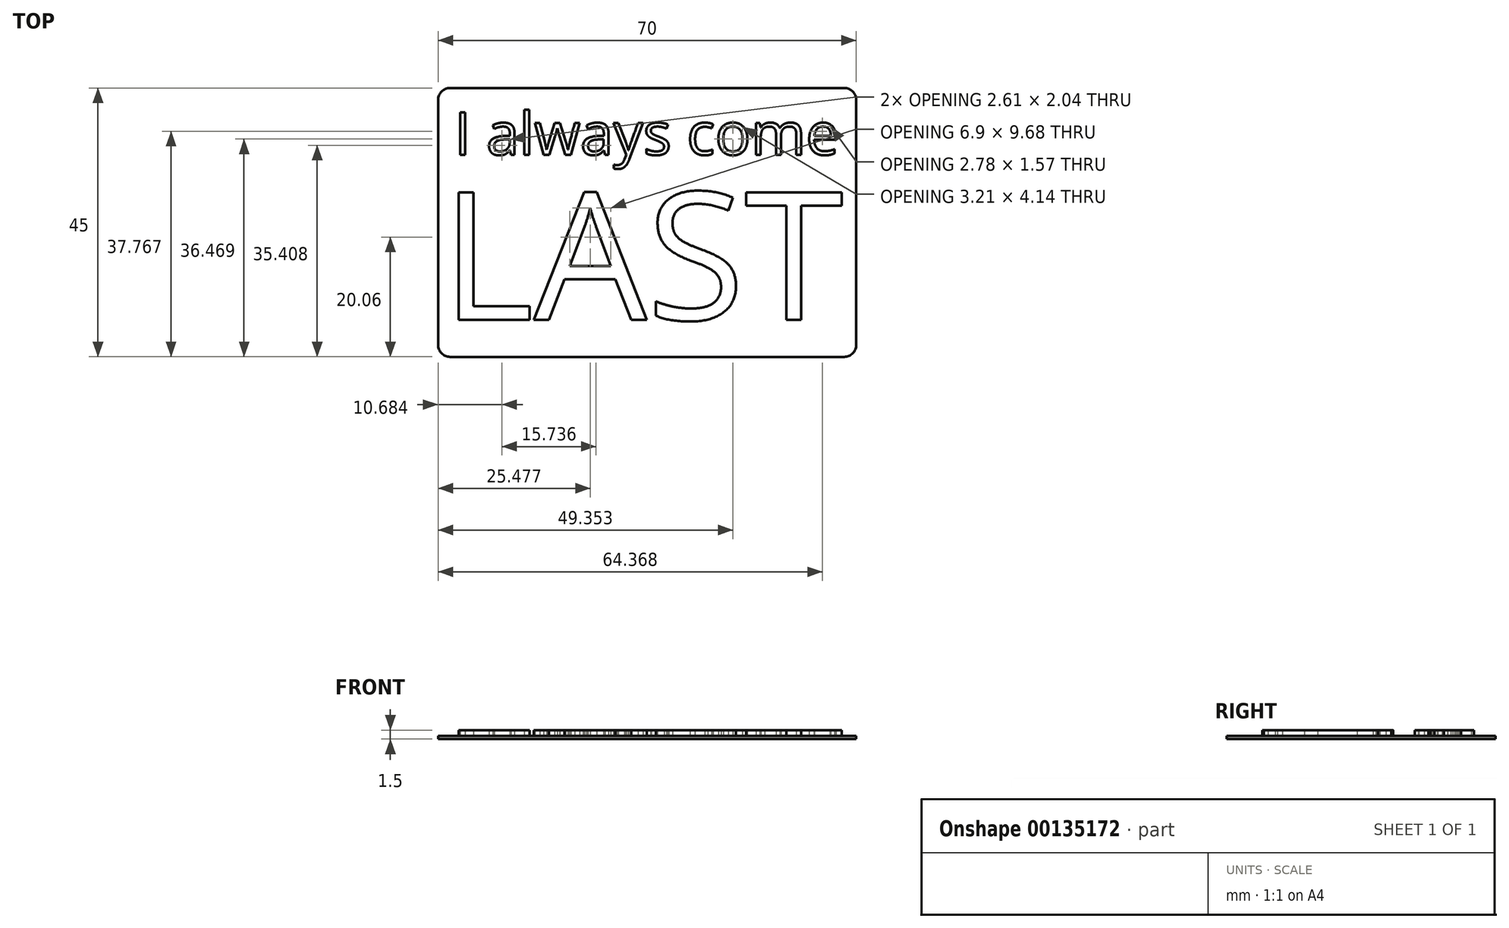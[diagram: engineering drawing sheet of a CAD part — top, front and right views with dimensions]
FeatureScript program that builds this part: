
annotation { "Feature Type Name" : "Feature", "Feature Type Description" : "" }
export const myFeature = defineFeature(function(context is Context, id is Id, definition is map)
    precondition{}
    {
        {
            var Q0;
            Q0=qCreatedBy(makeId("Top.planeOp"),FACE);
            var sketch = newSketch(context, id + "F0", { "sketchPlane" : qUnion([Q0])});
            skLineSegment(sketch, "E0.bottom", {"start": v(-20.28, 6.49) * mm, "end": v(49.72, 6.49) * mm});
            skLineSegment(sketch, "E0.top", {"start": v(-20.28, -38.51) * mm, "end": v(49.72, -38.51) * mm});
            skLineSegment(sketch, "E0.left", {"start": v(-20.28, 6.49) * mm, "end": v(-20.28, -38.51) * mm});
            skLineSegment(sketch, "E0.right", {"start": v(49.72, 6.49) * mm, "end": v(49.72, -38.51) * mm});
            skSolve(sketch);
        }
        {
            var Q0;
            Q0=makeQuery(id+"F0.imprint","IMPRINT",FACE,{"disambiguationData":[TD([[makeQuery(id+"F0.imprint","IMPRINT",EDGE,{"derivedFrom":sQuery(id+"F0.wireOp",EDGE,"E0.bottom")}),-1.0]])]});
            extrude(context, id + "F1", {"entities" : qUnion([Q0]), "oppositeDirection" : true, "depth" : 0.5 * mm});
        }
        {
            var Q0;
            Q0=makeQuery(id+"F1.opExtrude","SWEPT_EDGE",EDGE,{"disambiguationData":[OSD([sQuery(id+"F0.wireOp",EDGE,"E0.top"),sQuery(id+"F0.wireOp",EDGE,"E0.right")])]});
            var Q1;
            Q1=makeQuery(id+"F1.opExtrude","SWEPT_EDGE",EDGE,{"disambiguationData":[OSD([sQuery(id+"F0.wireOp",EDGE,"E0.top"),sQuery(id+"F0.wireOp",EDGE,"E0.left")])]});
            var Q2;
            Q2=makeQuery(id+"F1.opExtrude","SWEPT_EDGE",EDGE,{"disambiguationData":[OSD([sQuery(id+"F0.wireOp",EDGE,"E0.bottom"),sQuery(id+"F0.wireOp",EDGE,"E0.left")])]});
            var Q3;
            Q3=makeQuery(id+"F1.opExtrude","SWEPT_EDGE",EDGE,{"disambiguationData":[OSD([sQuery(id+"F0.wireOp",EDGE,"E0.bottom"),sQuery(id+"F0.wireOp",EDGE,"E0.right")])]});
            fillet(context, id + "F2", {"entities" : qUnion([Q0, Q1, Q2, Q3]), "radius" : 2 * mm, "tangentPropagation" : true, "allowEdgeOverflow" : false});
        }
        {
            var Q0;
            Q0=qCreatedBy(makeId("Top.planeOp"),FACE);
            var sketch = newSketch(context, id + "F3", { "sketchPlane" : qUnion([Q0])});
            skText(sketch, "E1", { "text": "LAST", "fontName": "OpenSans-Regular.ttf"});
            skPoint(sketch, "E2", {"position": v(14.72, -38.51) * mm});
            skText(sketch, "E3", { "text": "I always come", "fontName": "OpenSans-Regular.ttf"});
            skPoint(sketch, "E4", {"position": v(14.72, 6.49) * mm});
            const initialGuessF3  = {"E1": [-0.01976, -0.0323, 1, 0, 0.0215], "E3": [-0.01754, -0.00469, 1, 0, 0.00714]};
            skSetInitialGuess(sketch, initialGuessF3);
            skSolve(sketch);
        }
        {
            var Q0;
            Q0=qSketchRegion(id+"F3",true);
            extrude(context, id + "F4", {"entities" : qUnion([Q0]), "depth" : 1 * mm});
        }
    });
